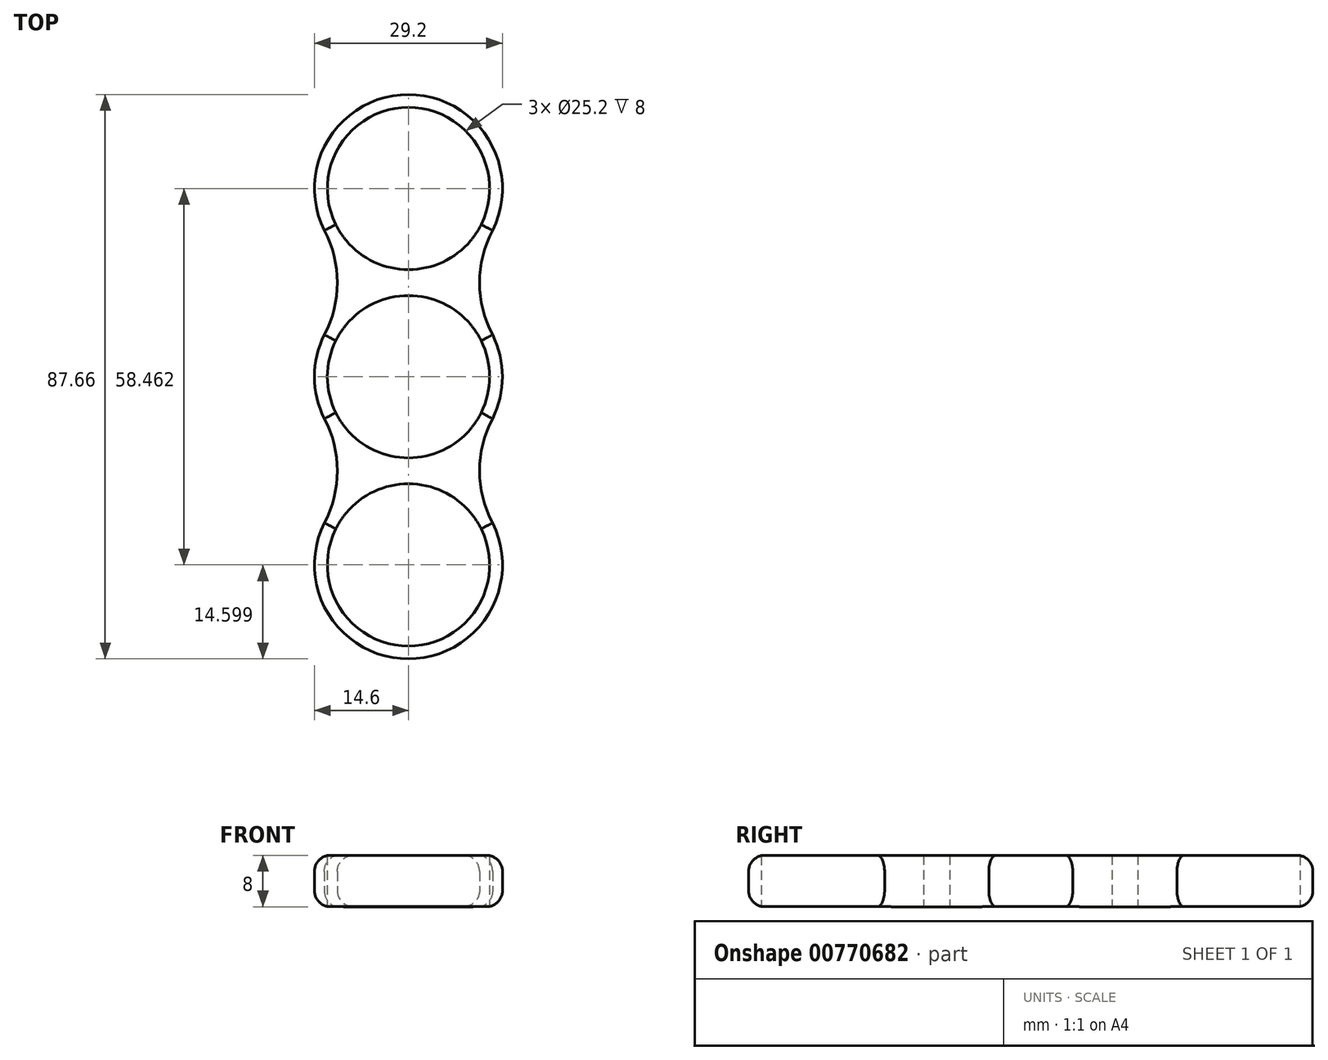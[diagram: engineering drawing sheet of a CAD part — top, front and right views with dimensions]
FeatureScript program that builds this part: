
annotation { "Feature Type Name" : "Feature", "Feature Type Description" : "" }
export const myFeature = defineFeature(function(context is Context, id is Id, definition is map)
    precondition{}
    {
        {
            var Q0;
            Q0=qCreatedBy(makeId("Top.planeOp"),FACE);
            var sketch = newSketch(context, id + "F0", { "sketchPlane" : qUnion([Q0])});
            skCircle(sketch, "E0", {"center": v(0, 0) * mm, "radius": 12.6 * mm});
            skArc(sketch, "E1", {"start": v(-12.87, 6.89) * mm, "mid": v(-14.6, 0) * mm, "end": v(-12.87, -6.89) * mm});
            skCircle(sketch, "E2", {"center": v(0, 29.23) * mm, "radius": 12.6 * mm});
            skArc(sketch, "E3", {"start": v(12.87, 22.34) * mm, "mid": v(0, 43.83) * mm, "end": v(-12.87, 22.34) * mm});
            skLineSegment(sketch, "E4", {"start": v(-14.6, 14.63) * mm, "end": v(-14.6, 14.62) * mm, "construction": true});
            skPoint(sketch, "E5.endSnap0", {"position": v(-14.6, 14.62) * mm});
            skArc(sketch, "E6", {"start": v(-13.06, 6.52) * mm, "mid": v(-11.04, 14.62) * mm, "end": v(-13.06, 22.71) * mm});
            skPoint(sketch, "E7.orphan", {"position": v(-14.6, 0) * mm});
            skPoint(sketch, "E8.orphan", {"position": v(-14.6, 29.23) * mm});
            skPoint(sketch, "E5.start.orphan", {"position": v(0, 14.63) * mm});
            skArc(sketch, "E9.MirrorCS", {"start": v(13.06, 6.52) * mm, "mid": v(11.04, 14.62) * mm, "end": v(13.06, 22.71) * mm});
            skArc(sketch, "E10.1.0", {"start": v(-12.87, -22.34) * mm, "mid": v(0, -43.83) * mm, "end": v(12.87, -22.34) * mm});
            skCircle(sketch, "E10.1.1", {"center": v(0, -29.23) * mm, "radius": 12.6 * mm});
            skArc(sketch, "E10.1.2", {"start": v(13.06, -6.52) * mm, "mid": v(11.04, -14.62) * mm, "end": v(13.06, -22.71) * mm});
            skArc(sketch, "E10.1.3", {"start": v(-13.06, -6.52) * mm, "mid": v(-11.04, -14.62) * mm, "end": v(-13.06, -22.71) * mm});
            skArc(sketch, "E11.trimOffspring", {"start": v(12.87, -6.89) * mm, "mid": v(14.6, 0) * mm, "end": v(12.87, 6.89) * mm});
            skSolve(sketch);
        }
        {
            var Q0;
            Q0=makeQuery(id+"F0.imprint","IMPRINT",FACE,{"disambiguationData":[TD([[makeQuery(id+"F0.imprint","IMPRINT",EDGE,{"derivedFrom":sQuery(id+"F0.wireOp",EDGE,"E0")}),-1.0]])]});
            extrude(context, id + "F1", {"entities" : qUnion([Q0]), "depth" : 8 * mm, "offsetDistance" : 25 * mm});
        }
        {
            var Q0;
            Q0=makeQuery(id+"F1.opExtrude","CAP_EDGE",EDGE,{"disambiguationData":[OSD([sQuery(id+"F0.wireOp",EDGE,"E3")])],"isStart":false});
            var Q1;
            Q1=makeQuery(id+"F1.opExtrude","CAP_EDGE",EDGE,{"disambiguationData":[OSD([sQuery(id+"F0.wireOp",EDGE,"E6")])],"isStart":false});
            var Q2;
            Q2=makeQuery(id+"F1.opExtrude","CAP_EDGE",EDGE,{"disambiguationData":[OSD([sQuery(id+"F0.wireOp",EDGE,"E9.MirrorCS")])],"isStart":false});
            var Q3;
            Q3=makeQuery(id+"F1.opExtrude","CAP_EDGE",EDGE,{"disambiguationData":[OSD([sQuery(id+"F0.wireOp",EDGE,"E11.trimOffspring")])],"isStart":false});
            var Q4;
            Q4=makeQuery(id+"F1.opExtrude","CAP_EDGE",EDGE,{"disambiguationData":[OSD([sQuery(id+"F0.wireOp",EDGE,"E1")])],"isStart":false});
            var Q5;
            Q5=makeQuery(id+"F1.opExtrude","CAP_EDGE",EDGE,{"disambiguationData":[OSD([sQuery(id+"F0.wireOp",EDGE,"E10.1.3")])],"isStart":false});
            var Q6;
            Q6=makeQuery(id+"F1.opExtrude","CAP_EDGE",EDGE,{"disambiguationData":[OSD([sQuery(id+"F0.wireOp",EDGE,"E10.1.0")])],"isStart":false});
            var Q7;
            Q7=makeQuery(id+"F1.opExtrude","CAP_EDGE",EDGE,{"disambiguationData":[OSD([sQuery(id+"F0.wireOp",EDGE,"E10.1.2")])],"isStart":false});
            var Q8;
            Q8=makeQuery(id+"F1.opExtrude","CAP_EDGE",EDGE,{"disambiguationData":[OSD([sQuery(id+"F0.wireOp",EDGE,"E10.1.0")])],"isStart":true});
            var Q9;
            Q9=makeQuery(id+"F1.opExtrude","CAP_EDGE",EDGE,{"disambiguationData":[OSD([sQuery(id+"F0.wireOp",EDGE,"E10.1.3")])],"isStart":true});
            var Q10;
            Q10=makeQuery(id+"F1.opExtrude","CAP_EDGE",EDGE,{"disambiguationData":[OSD([sQuery(id+"F0.wireOp",EDGE,"E10.1.2")])],"isStart":true});
            var Q11;
            Q11=makeQuery(id+"F1.opExtrude","CAP_EDGE",EDGE,{"disambiguationData":[OSD([sQuery(id+"F0.wireOp",EDGE,"E11.trimOffspring")])],"isStart":true});
            var Q12;
            Q12=makeQuery(id+"F1.opExtrude","CAP_EDGE",EDGE,{"disambiguationData":[OSD([sQuery(id+"F0.wireOp",EDGE,"E9.MirrorCS")])],"isStart":true});
            var Q13;
            Q13=makeQuery(id+"F1.opExtrude","CAP_EDGE",EDGE,{"disambiguationData":[OSD([sQuery(id+"F0.wireOp",EDGE,"E3")])],"isStart":true});
            var Q14;
            Q14=makeQuery(id+"F1.opExtrude","CAP_EDGE",EDGE,{"disambiguationData":[OSD([sQuery(id+"F0.wireOp",EDGE,"E6")])],"isStart":true});
            var Q15;
            Q15=makeQuery(id+"F1.opExtrude","CAP_EDGE",EDGE,{"disambiguationData":[OSD([sQuery(id+"F0.wireOp",EDGE,"E1")])],"isStart":true});
            fillet(context, id + "F2", {"entities" : qUnion([Q0, Q1, Q2, Q3, Q4, Q5, Q6, Q7, Q8, Q9, Q10, Q11, Q12, Q13, Q14, Q15]), "radius" : 2.5 * mm, "tangentPropagation" : true, "allowEdgeOverflow" : false});
        }
    });
